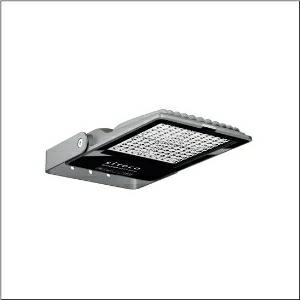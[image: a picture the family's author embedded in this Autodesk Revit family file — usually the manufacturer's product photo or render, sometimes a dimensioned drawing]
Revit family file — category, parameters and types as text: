
# Revit family: sicompact_r__31_mini___pl32_5xa7571f2k23_7a3f
name_source: partatom
category: Lighting Fixtures
units: mm (PartAtom-declared; Revit-internal decimal feet)

## family parameters
Cut with Voids When Loaded = No
Host = Face
Light Source = No
Part Type = Normal
Room Calculation Point = No
Round Connector Dimension = Use Diameter
Shared = No

## types (1)
- SiCompact® 31 mini  PL32 (1 x LED, 20000 lm, 130 W, 4000K)
    Apparent Load = 130 VA
    CIE Flux Codes = 32 69 98 100 100
    Color Rendering = 70
    Color Temperature = 4000K
    Default Elevation = 1800 mm
    Description = SiCompact® 31 mini, floodlight, primary light control with lens, of plastic, of toughened safety glass, transparent, light distribution: PL32, light emission: direct distribution, primary light characteristic: asymmetric, installation type: surface-mounted, LED, High Power LED, rated luminous flux: 20.000lm, luminous efficacy: 154lm/W, light colour: 740, colour temperature: 4000K, control gear: ECG, with cable, 3x 1.5mm², mains connection: 220..240V, AC, 50/60Hz, connection cable pre-assembled, cable length: 2m, rated input power: 130W, of diecast aluminium, specular, metallic grey (RAL 9006), length: 461mm, width: 261mm, height: 62mm, bracket, of sheet steel, coated, metallic grey (RAL 9006), ON/OFF, protection rating (complete): IP66, insulation class (complete): insulation class I (protective earthing), certification: CE, impact resistance: IK08, permissible operating ambient temperature: -40..+45°C, packaging unit: 1 piece

Light Distribution: PL32
    Height = 62 mm  [stored 0.203412 ft]
    Lamp = 1 x LED
    Lamp Light Flux = 20000 lm
    Lamp Power = 130 W
    Lamp count = 1
    Length = 460 mm
    Luminous efficacy = 154 lm/W
    Manufacturer = Siteco
    ModVariant = No
    Model = 5XA7571F2K23
    Number of Poles = 1
    OnlyDefault = Yes
    Power Factor = 1
    Product Name = SiCompact® 31 mini | PL32
    Product group = floodlight | pylon top
    ProductGroupID = 6101
    Protection Class = Protection class I
    Protection Degree = IP 66
    RLX_Detail_Level = 1
    RlxData = <blob elided: 126437 chars, md5=91c60a8b>
    Socket = socket
    Standby Power = 0 W
    System Light Flux = 20000 lm
    System Power = 130 W
    Type Comments = Product without accessories
    Type Image = l_1006951.jpg
    URL = http://relux.com
    VarID = ---
    Voltage = 0 V
    Weight = 0.00 kg
    Width = 260 mm

note: [stored X ft] marks values corroborated as IEEE doubles in the binary element streams (Revit-internal decimal feet)

## geometry (parser evidence)
native form markers: Blend x4, Sweep x15
no freeform markers — native parametric forms only
